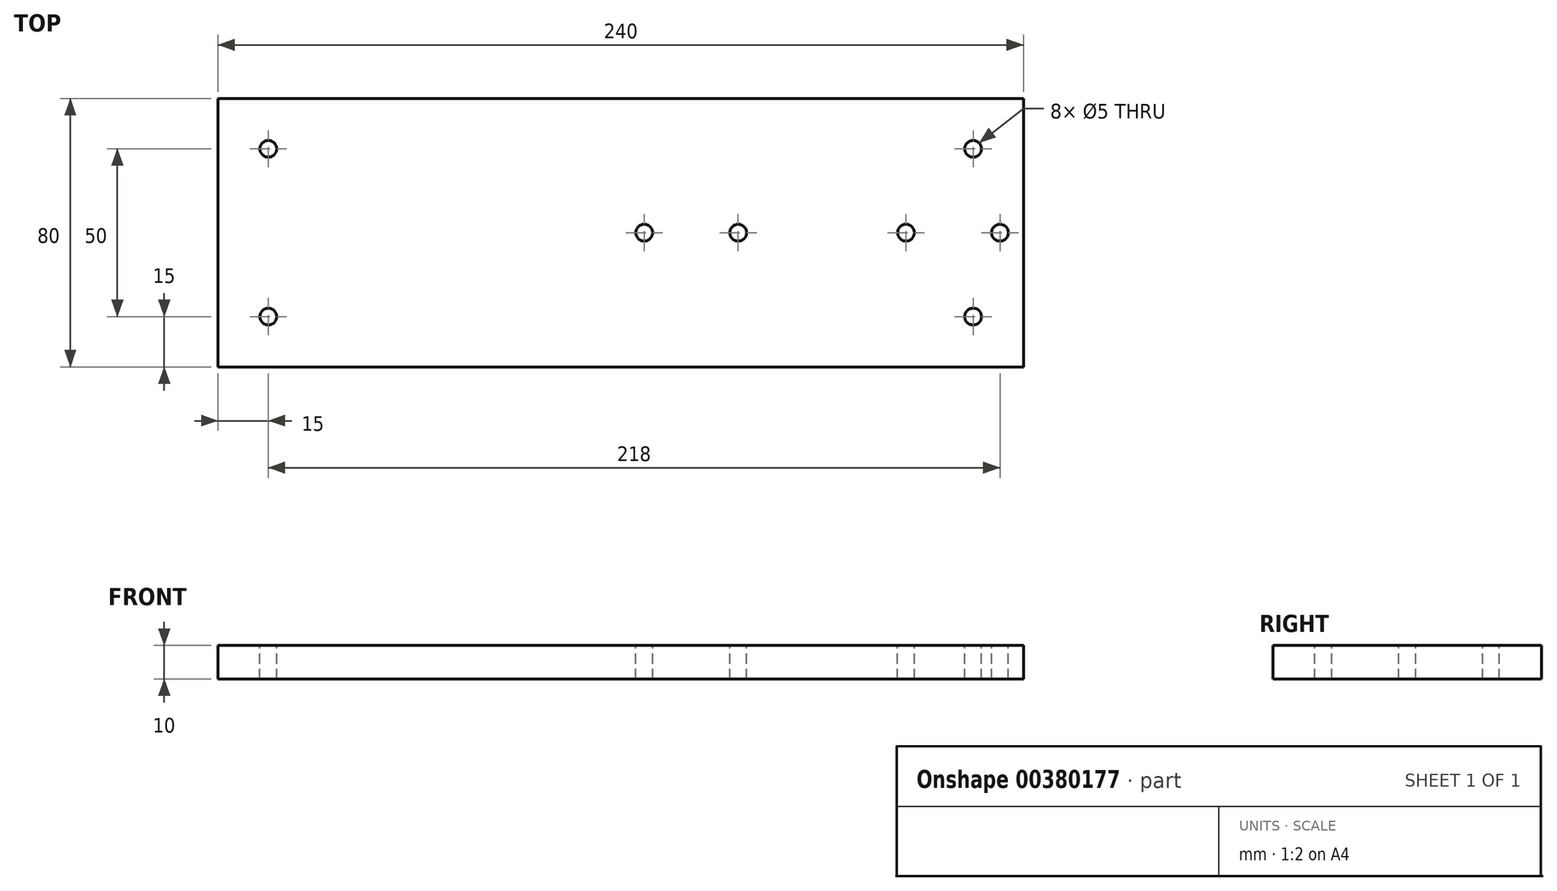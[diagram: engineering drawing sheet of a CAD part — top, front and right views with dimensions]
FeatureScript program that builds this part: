
annotation { "Feature Type Name" : "Feature", "Feature Type Description" : "" }
export const myFeature = defineFeature(function(context is Context, id is Id, definition is map)
    precondition{}
    {
        {
            var Q0;
            Q0=qCreatedBy(makeId("Top.planeOp"),FACE);
            var sketch = newSketch(context, id + "F0", { "sketchPlane" : qUnion([Q0])});
            skLineSegment(sketch, "E0.bottom", {"start": v(-120, 40) * mm, "end": v(120, 40) * mm});
            skLineSegment(sketch, "E0.top", {"start": v(-120, -40) * mm, "end": v(120, -40) * mm});
            skLineSegment(sketch, "E0.left", {"start": v(-120, 40) * mm, "end": v(-120, -40) * mm});
            skLineSegment(sketch, "E0.right", {"start": v(120, 40) * mm, "end": v(120, -40) * mm});
            skSolve(sketch);
        }
        {
            var Q0;
            Q0=makeQuery(id+"F0.imprint","IMPRINT",FACE,{"disambiguationData":[TD([[makeQuery(id+"F0.imprint","IMPRINT",EDGE,{"derivedFrom":sQuery(id+"F0.wireOp",EDGE,"E0.bottom")}),-1.0]])]});
            extrude(context, id + "F1", {"entities" : qUnion([Q0]), "depth" : 10 * mm});
        }
        {
            var Q0;
            Q0=makeQuery(id+"F1.opExtrude","CAP_FACE",FACE,{"disambiguationData":[OSD([sQuery(id+"F0.wireOp",EDGE,"E0.bottom"),sQuery(id+"F0.wireOp",EDGE,"E0.top"),sQuery(id+"F0.wireOp",EDGE,"E0.left"),sQuery(id+"F0.wireOp",EDGE,"E0.right")])],"isStart":false});
            var sketch = newSketch(context, id + "F2", { "sketchPlane" : qUnion([Q0])});
            skPoint(sketch, "E1", {"position": v(105, 25) * mm});
            skPoint(sketch, "E2", {"position": v(105, -25) * mm});
            skPoint(sketch, "E3", {"position": v(-105, -25) * mm});
            skPoint(sketch, "E4", {"position": v(-105, 25) * mm});
            skPoint(sketch, "E5", {"position": v(113, 0) * mm});
            skPoint(sketch, "E6", {"position": v(85, 0) * mm});
            skPoint(sketch, "E7", {"position": v(35, 0) * mm});
            skPoint(sketch, "E8", {"position": v(7, 0) * mm});
            skSolve(sketch);
        }
        {
            var Q0;
            Q0=sQuery(id+"F2.wireOp",VERTEX,"E4");
            var Q1;
            Q1=sQuery(id+"F2.wireOp",VERTEX,"E3");
            var Q2;
            Q2=sQuery(id+"F2.wireOp",VERTEX,"E1");
            var Q3;
            Q3=sQuery(id+"F2.wireOp",VERTEX,"E2");
            var Q4;
            Q4=sQuery(id+"F2.wireOp",VERTEX,"E8");
            var Q5;
            Q5=sQuery(id+"F2.wireOp",VERTEX,"E7");
            var Q6;
            Q6=sQuery(id+"F2.wireOp",VERTEX,"E6");
            var Q7;
            Q7=sQuery(id+"F2.wireOp",VERTEX,"E5");
            var Q8;
            Q8=makeQuery(id+"F1.opExtrude","SWEPT_BODY",BODY,{"disambiguationData":[OSD([sQuery(id+"F0.wireOp",EDGE,"E0.bottom"),sQuery(id+"F0.wireOp",EDGE,"E0.top"),sQuery(id+"F0.wireOp",EDGE,"E0.left"),sQuery(id+"F0.wireOp",EDGE,"E0.right")])]});
            hole(context, id + "F3", {"style" : HoleStyle.SIMPLE, "endStyle" : HoleEndStyle.THROUGH, "holeDiameter" : 5 * mm, "isTappedThrough" : true, "tappedDepth" : 12.7 * mm, "tapClearance" : 3, "locations" : qUnion([Q0, Q1, Q2, Q3, Q4, Q5, Q6, Q7]), "scope" : qUnion([Q8])});
        }
    });
